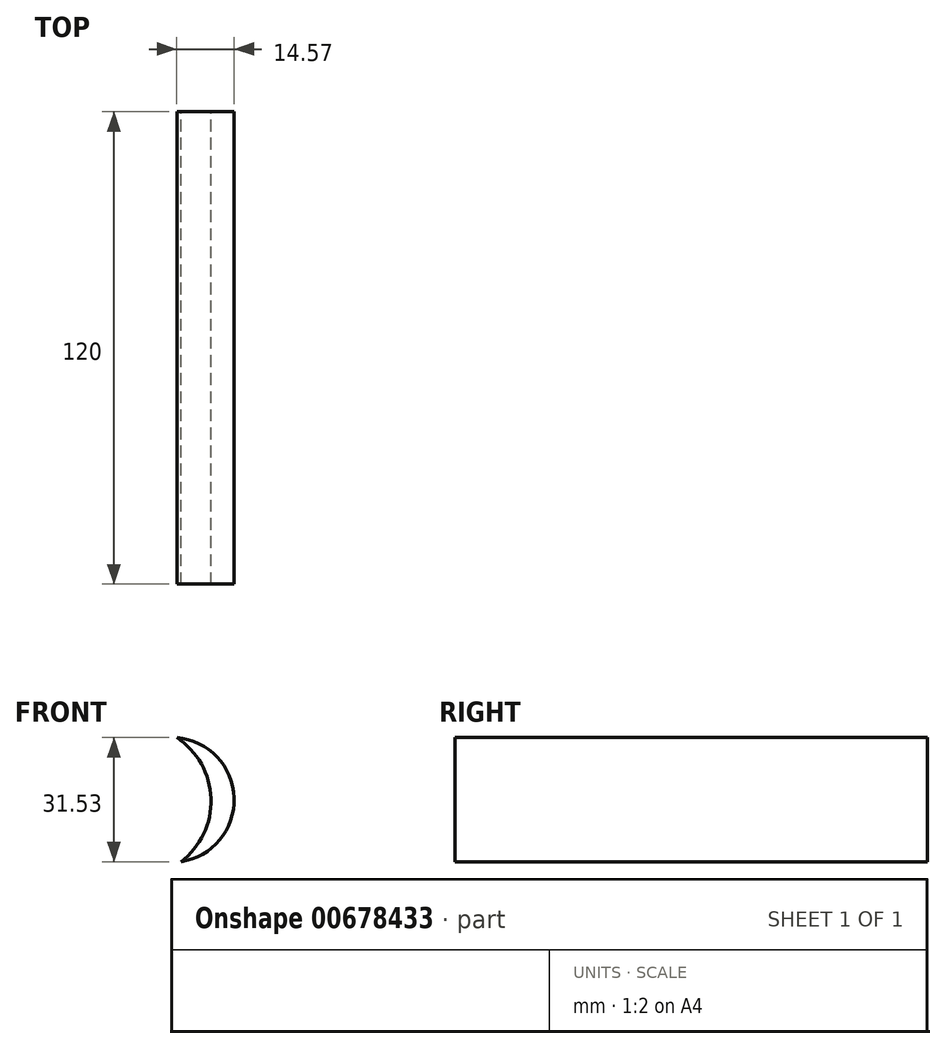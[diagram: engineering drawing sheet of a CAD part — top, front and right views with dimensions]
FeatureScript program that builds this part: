
annotation { "Feature Type Name" : "Feature", "Feature Type Description" : "" }
export const myFeature = defineFeature(function(context is Context, id is Id, definition is map)
    precondition{}
    {
        {
            var Q0;
            Q0=qCreatedBy(makeId("Front.planeOp"),FACE);
            var sketch = newSketch(context, id + "F0", { "sketchPlane" : qUnion([Q0])});
            skArc(sketch, "E0", {"start": v(-6.66, -16) * mm, "mid": v(6.86, 0.23) * mm, "end": v(-7.7, 15.53) * mm});
            skArc(sketch, "E1", {"start": v(-6.66, -16) * mm, "mid": v(0.98, 0.03) * mm, "end": v(-7.7, 15.53) * mm});
            skCircle(sketch, "E2", {"center": v(0, 0) * mm, "radius": 25.5 * mm});
            skSolve(sketch);
        }
        {
            var Q0;
            Q0=makeQuery(id+"F0.imprint","IMPRINT",FACE,{"disambiguationData":[TD([[makeQuery(id+"F0.imprint","IMPRINT",EDGE,{"derivedFrom":sQuery(id+"F0.wireOp",EDGE,"E0")}),1.0]])]});
            var Q1;
            Q1=sQuery(id+"F0.wireOp",EDGE,"E0");
            var Q2;
            Q2=sQuery(id+"F0.wireOp",EDGE,"E1");
            extrude(context, id + "F1", {"entities" : qUnion([Q0]), "surfaceOperationType" : NewSurfaceOperationType.ADD, "surfaceEntities" : qUnion([Q1, Q2]), "depth" : 120 * mm, "offsetDistance" : 25 * mm});
        }
    });
